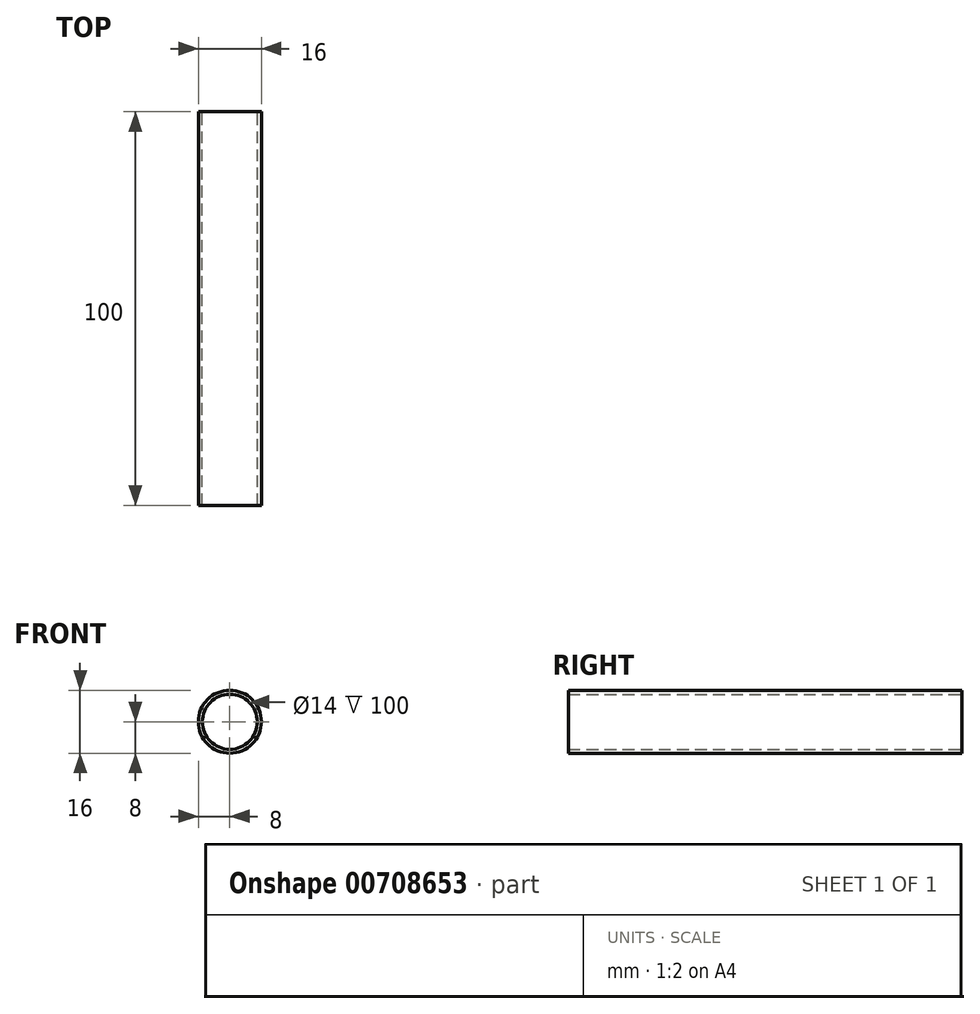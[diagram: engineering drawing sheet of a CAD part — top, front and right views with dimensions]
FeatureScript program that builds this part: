
annotation { "Feature Type Name" : "Feature", "Feature Type Description" : "" }
export const myFeature = defineFeature(function(context is Context, id is Id, definition is map)
    precondition{}
    {
        {
            var Q0;
            Q0=qCreatedBy(makeId("Front.planeOp"),FACE);
            var sketch = newSketch(context, id + "F0", { "sketchPlane" : qUnion([Q0])});
            skCircle(sketch, "E0", {"center": v(0, 0) * mm, "radius": 8 * mm});
            skCircle(sketch, "E1", {"center": v(0, 0) * mm, "radius": 7 * mm});
            skSolve(sketch);
        }
        {
            var Q0;
            Q0=makeQuery(id+"F0.imprint","IMPRINT",FACE,{"disambiguationData":[TD([[makeQuery(id+"F0.imprint","IMPRINT",EDGE,{"derivedFrom":sQuery(id+"F0.wireOp",EDGE,"E0")}),1.0]])]});
            extrude(context, id + "F1", {"entities" : qUnion([Q0]), "depth" : 100 * mm, "offsetDistance" : 25 * mm});
        }
    });
